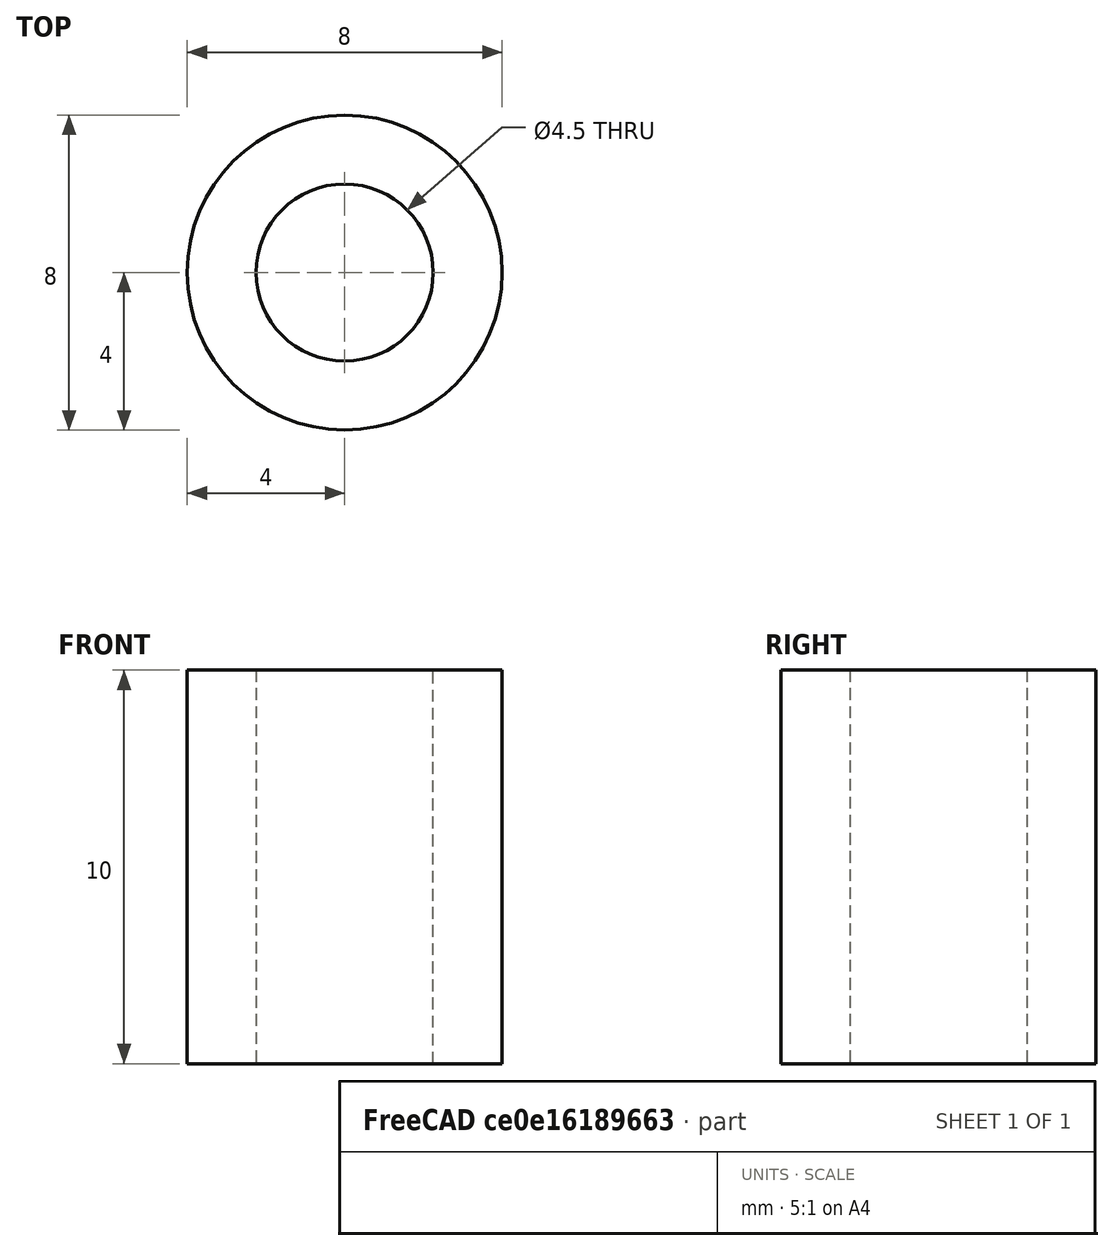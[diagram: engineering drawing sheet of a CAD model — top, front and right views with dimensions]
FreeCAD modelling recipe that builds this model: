
FCSTD DOCUMENT  (FreeCAD 0.19R24366 (Git))
Label: spacers
License: All rights reserved
LicenseURL: http://en.wikipedia.org/wiki/All_rights_reserved
objects: Sketcher::SketchObject×1, PartDesign::Pad×1, PartDesign::Body×1, Mesh::Feature×1
note: 4 computed .brp shape members not serialized (recipe doc carries the construction recipe); baked Part::Feature solids carry a one-line shape summary decoded from their .brp

FEATURE [Sketcher::SketchObject] Sketch
  FullyConstrained = true
  MapMode = 5
  Support = -> [XY_Plane]
  sketch-geometry (2):
    g0: Circle CenterX=0 CenterY=0 CenterZ=0 NormalX=0 NormalY=0 NormalZ=1 AngleXU=0 Radius=2.25
    g1: Circle CenterX=0 CenterY=0 CenterZ=0 NormalX=0 NormalY=0 NormalZ=1 AngleXU=0 Radius=4
  constraints (4):
    c: Coincident(g0,g-1)
    c: Coincident(g1,g0)
    c: Diameter(g0) = 4.5
    c: Diameter(g1) = 8
FEATURE [PartDesign::Pad] Pad
  Direction = (1,1,1)
  Length = 10
  Length2 = 100
  Profile = -> Sketch
  Refine = true
  Type = 0
FEATURE [PartDesign::Body] Body
  Group = -> [Sketch,Pad]
  Origin = -> Origin
  Tip = -> Pad
FEATURE [Mesh::Feature] Mesh  label="Body (Meshed)"
